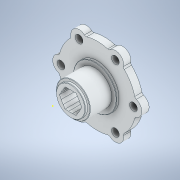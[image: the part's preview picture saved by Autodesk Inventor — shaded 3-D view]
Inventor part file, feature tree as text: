
AUTODESK INVENTOR PART (.ipt)
format: ipt  version: 2020 (Build 240168000, 168)  size: 221,184 bytes
history: native  units: in
note: dims shown in document units (in); Inventor stores cm internally (conversion verified against a paired STEP export)
features: sketch x1, other x1
ambient origin geometry x8: Origin, YZ Plane, XZ Plane, XY Plane, X Axis, Y Axis, Z Axis, Center Point
bodies: Solid1 (feature_tree)
feature tree (2):
  sketch  "Sketch1"
  other  "_2019 Hub Designer_-_Fillet1_"
